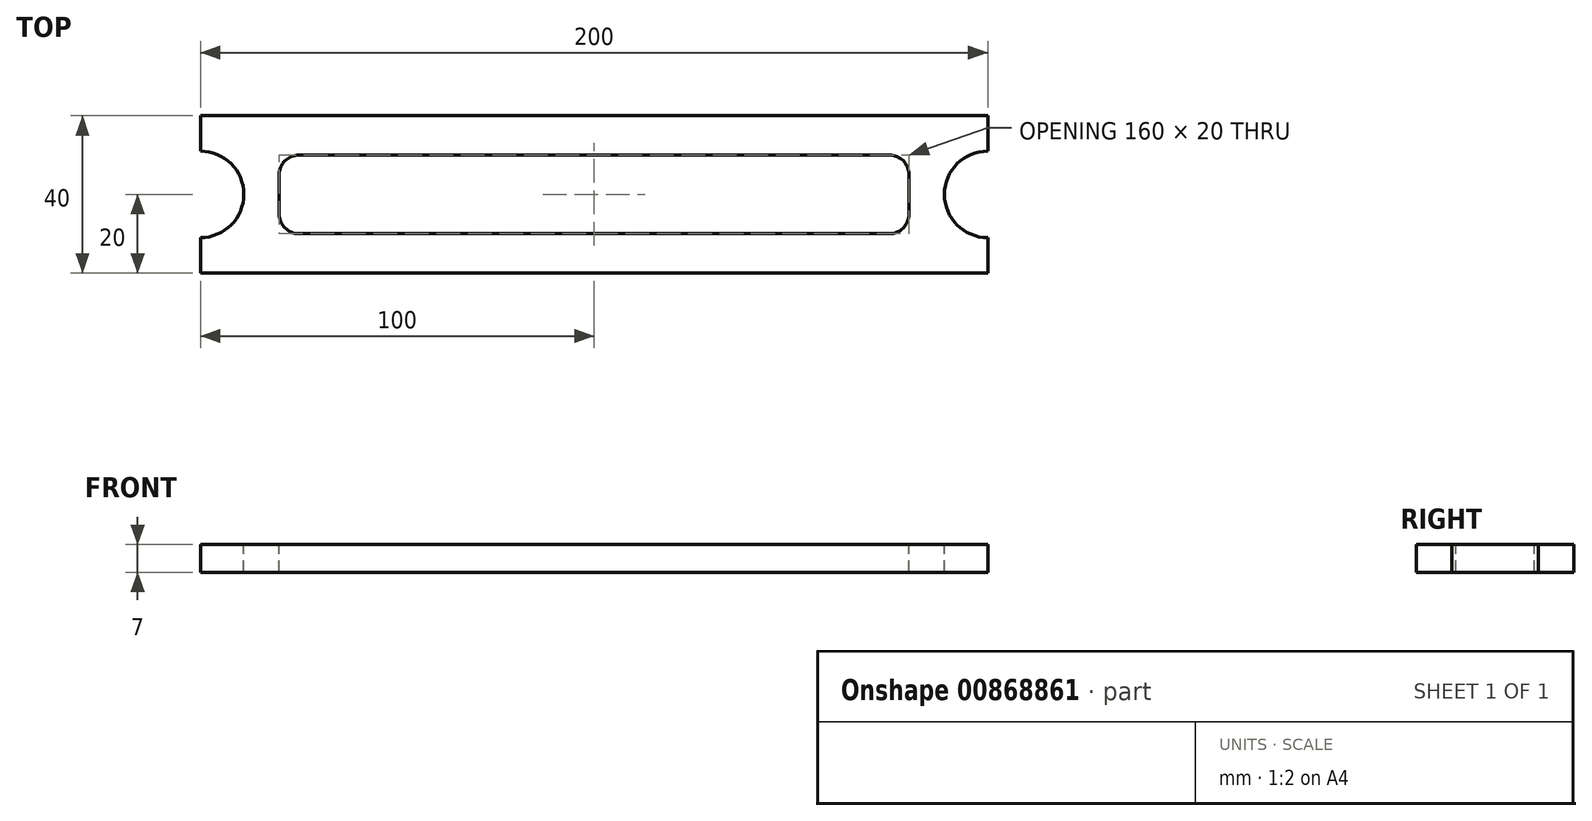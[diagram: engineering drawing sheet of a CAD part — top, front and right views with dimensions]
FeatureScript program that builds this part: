
annotation { "Feature Type Name" : "Feature", "Feature Type Description" : "" }
export const myFeature = defineFeature(function(context is Context, id is Id, definition is map)
    precondition{}
    {
        {
            var Q0;
            Q0=qCreatedBy(makeId("Top.planeOp"),FACE);
            var sketch = newSketch(context, id + "F0", { "sketchPlane" : qUnion([Q0])});
            skLineSegment(sketch, "E0.bottom", {"start": v(0, 0) * mm, "end": v(200, 0) * mm});
            skLineSegment(sketch, "E0.top", {"start": v(0, 40) * mm, "end": v(200, 40) * mm});
            skLineSegment(sketch, "E0.left", {"start": v(0, 0) * mm, "end": v(0, 40) * mm});
            skLineSegment(sketch, "E0.right", {"start": v(200, 0) * mm, "end": v(200, 40) * mm});
            skArc(sketch, "E1", {"start": v(0, 0) * mm, "mid": v(-20, 20) * mm, "end": v(0, 40) * mm});
            skArc(sketch, "E2", {"start": v(200, 40) * mm, "mid": v(220, 20) * mm, "end": v(200, 0) * mm});
            skCircle(sketch, "E3", {"center": v(0, 20) * mm, "radius": 10 * mm});
            skCircle(sketch, "E4", {"center": v(200, 20) * mm, "radius": 10 * mm});
            skSolve(sketch);
        }
        {
            var Q0;
            {var subQ5=sQuery(id+"F0.wireOp",EDGE,"E0.bottom");Q0=makeQuery(id+"F0.imprint","IMPRINT",FACE,{"disambiguationData":[TD([[makeQuery(id+"F0.imprint","IMPRINT",EDGE,{"derivedFrom":subQ5}),1.0]])]});}
            var Q1;
            {var subQ0=sQuery(id+"F0.wireOp",EDGE,"E1");Q1=makeQuery(id+"F0.imprint","IMPRINT",FACE,{"disambiguationData":[TD([[makeQuery(id+"F0.imprint","IMPRINT",EDGE,{"derivedFrom":subQ0}),-1.0]])]});}
            var Q2;
            {var subQ0=sQuery(id+"F0.wireOp",EDGE,"E2");Q2=makeQuery(id+"F0.imprint","IMPRINT",FACE,{"disambiguationData":[TD([[makeQuery(id+"F0.imprint","IMPRINT",EDGE,{"derivedFrom":subQ0}),-1.0]])]});}
            extrude(context, id + "F1", {"entities" : qUnion([Q0, Q1, Q2]), "depth" : 7 * mm, "offsetDistance" : 25 * mm});
        }
        {
            var Q0;
            Q0=makeQuery(id+"F1.opExtrude","CAP_FACE",FACE,{"disambiguationData":[OSD([sQuery(id+"F0.wireOp",EDGE,"E0.bottom"),sQuery(id+"F0.wireOp",EDGE,"E0.top"),sQuery(id+"F0.wireOp",EDGE,"E1"),sQuery(id+"F0.wireOp",EDGE,"E2"),sQuery(id+"F0.wireOp",EDGE,"E3"),sQuery(id+"F0.wireOp",EDGE,"E4")])],"isStart":false});
            var sketch = newSketch(context, id + "F2", { "sketchPlane" : qUnion([Q0])});
            skCircle(sketch, "E5", {"center": v(0, 20) * mm, "radius": 11 * mm});
            skCircle(sketch, "E6", {"center": v(200, 20) * mm, "radius": 11 * mm});
            skSolve(sketch);
        }
        {
            var Q0;
            Q0=makeQuery(id+"F2.imprint","IMPRINT",FACE,{"disambiguationData":[TD([[makeQuery(id+"F2.imprint","IMPRINT",EDGE,{"derivedFrom":sQuery(id+"F2.wireOp",EDGE,"E5")}),1.0]])]});
            var Q1;
            Q1=makeQuery(id+"F2.imprint","IMPRINT",FACE,{"disambiguationData":[TD([[makeQuery(id+"F2.imprint","IMPRINT",EDGE,{"derivedFrom":sQuery(id+"F2.wireOp",EDGE,"E6")}),1.0]])]});
            extrude(context, id + "F3", {"entities" : qUnion([Q0, Q1]), "operationType" : NewBodyOperationType.REMOVE, "oppositeDirection" : true, "depth" : 7 * mm, "offsetDistance" : 25 * mm});
        }
        {
            var Q0;
            Q0=makeQuery(id+"F1.opExtrude","CAP_FACE",FACE,{"disambiguationData":[OSD([sQuery(id+"F0.wireOp",EDGE,"E0.bottom"),sQuery(id+"F0.wireOp",EDGE,"E0.top"),sQuery(id+"F0.wireOp",EDGE,"E1"),sQuery(id+"F0.wireOp",EDGE,"E2"),sQuery(id+"F0.wireOp",EDGE,"E3"),sQuery(id+"F0.wireOp",EDGE,"E4")])],"isStart":false});
            var sketch = newSketch(context, id + "F4", { "sketchPlane" : qUnion([Q0])});
            skLineSegment(sketch, "E7", {"start": v(0, 40) * mm, "end": v(20, 40) * mm});
            skLineSegment(sketch, "E8", {"start": v(200, 0) * mm, "end": v(180, 0) * mm});
            skLineSegment(sketch, "E9", {"start": v(20, 40) * mm, "end": v(20, 30) * mm});
            skLineSegment(sketch, "E10", {"start": v(180, 0) * mm, "end": v(180, 10) * mm});
            skLineSegment(sketch, "E11.bottom", {"start": v(20, 30) * mm, "end": v(180, 30) * mm});
            skLineSegment(sketch, "E11.top", {"start": v(20, 10) * mm, "end": v(180, 10) * mm});
            skLineSegment(sketch, "E11.left", {"start": v(20, 30) * mm, "end": v(20, 10) * mm});
            skLineSegment(sketch, "E11.right", {"start": v(180, 30) * mm, "end": v(180, 10) * mm});
            skSolve(sketch);
        }
        {
            var Q0;
            Q0=makeQuery(id+"F4.imprint","IMPRINT",FACE,{"disambiguationData":[TD([[makeQuery(id+"F4.imprint","IMPRINT",EDGE,{"derivedFrom":sQuery(id+"F4.wireOp",EDGE,"E11.bottom")}),-1.0]])]});
            extrude(context, id + "F5", {"entities" : qUnion([Q0]), "operationType" : NewBodyOperationType.REMOVE, "endBound" : BoundingType.THROUGH_ALL, "oppositeDirection" : true, "depth" : 25 * mm, "offsetDistance" : 25 * mm});
        }
        {
            var Q0;
            Q0=makeQuery(id+"F5.boolean.opBoolean","COPY",EDGE,{"derivedFrom":makeQuery(id+"F5.opExtrude","SWEPT_EDGE",EDGE,{"disambiguationData":[OSD([sQuery(id+"F4.wireOp",EDGE,"E9"),sQuery(id+"F4.wireOp",EDGE,"E11.bottom"),sQuery(id+"F4.wireOp",EDGE,"E11.left")])]})});
            var Q1;
            Q1=makeQuery(id+"F5.boolean.opBoolean","COPY",EDGE,{"derivedFrom":makeQuery(id+"F5.opExtrude","SWEPT_EDGE",EDGE,{"disambiguationData":[OSD([sQuery(id+"F4.wireOp",EDGE,"E11.bottom"),sQuery(id+"F4.wireOp",EDGE,"E11.right")])]})});
            var Q2;
            Q2=makeQuery(id+"F5.boolean.opBoolean","COPY",EDGE,{"derivedFrom":makeQuery(id+"F5.opExtrude","SWEPT_EDGE",EDGE,{"disambiguationData":[OSD([sQuery(id+"F4.wireOp",EDGE,"E10"),sQuery(id+"F4.wireOp",EDGE,"E11.top"),sQuery(id+"F4.wireOp",EDGE,"E11.right")])]})});
            var Q3;
            Q3=makeQuery(id+"F5.boolean.opBoolean","COPY",EDGE,{"derivedFrom":makeQuery(id+"F5.opExtrude","SWEPT_EDGE",EDGE,{"disambiguationData":[OSD([sQuery(id+"F4.wireOp",EDGE,"E11.top"),sQuery(id+"F4.wireOp",EDGE,"E11.left")])]})});
            fillet(context, id + "F6", {"entities" : qUnion([Q0, Q1, Q2, Q3]), "radius" : 5 * mm, "tangentPropagation" : true, "allowEdgeOverflow" : false});
        }
    });
